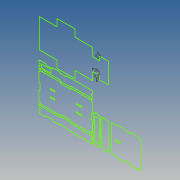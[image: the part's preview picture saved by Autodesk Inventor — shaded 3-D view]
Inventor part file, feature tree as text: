
AUTODESK INVENTOR PART (.ipt)
format: ipt  version: 2020 (Build 240168000, 168)  size: 147,456 bytes
history: native  units: mm
features: sketch x1
ambient origin geometry x8: Origin, YZ Plane, XZ Plane, XY Plane, X Axis, Y Axis, Z Axis, Center Point
feature tree (1):
  sketch  "Sketch1"  dims[d302=20.0mm d303=0.5mm d304=0.5mm]
